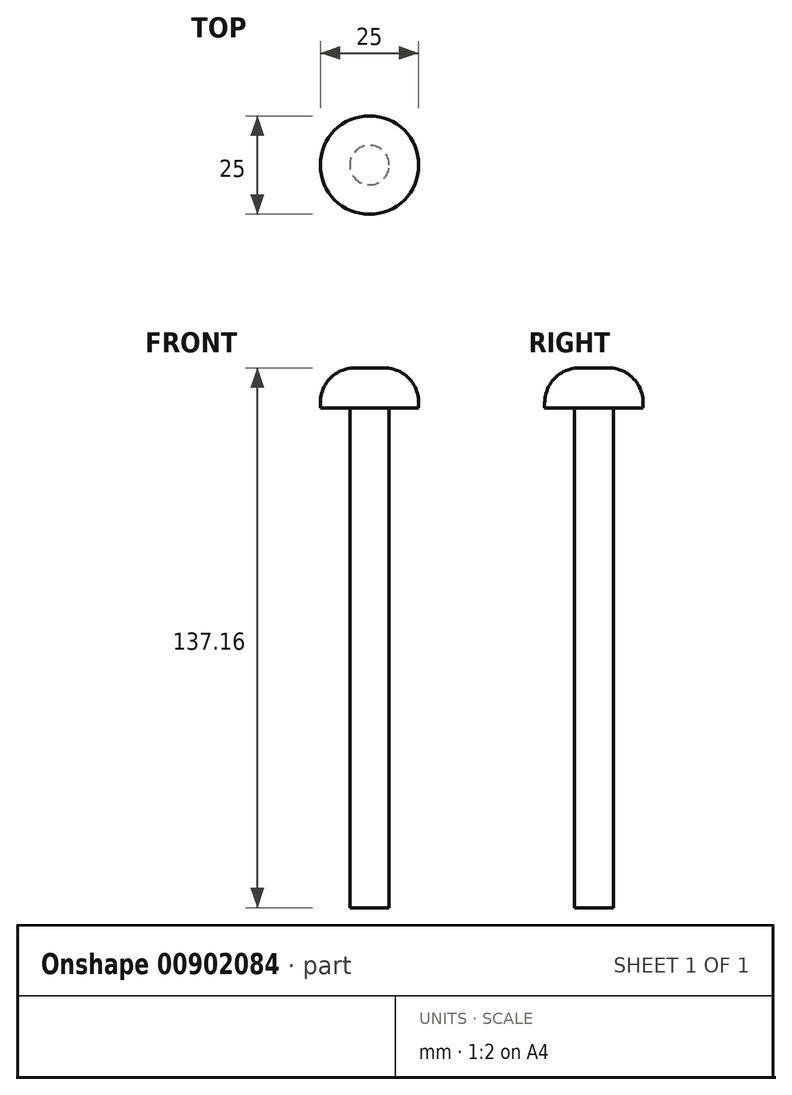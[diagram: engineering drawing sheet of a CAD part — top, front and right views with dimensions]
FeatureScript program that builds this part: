
annotation { "Feature Type Name" : "Feature", "Feature Type Description" : "" }
export const myFeature = defineFeature(function(context is Context, id is Id, definition is map)
    precondition{}
    {
        {
            var Q0;
            Q0=qCreatedBy(makeId("Top.planeOp"),FACE);
            var sketch = newSketch(context, id + "F0", { "sketchPlane" : qUnion([Q0])});
            skCircle(sketch, "E0", {"center": v(0, 0) * mm, "radius": 5 * mm});
            skSolve(sketch);
        }
        {
            var Q0;
            Q0=qSketchRegion(id+"F0",true);
            extrude(context, id + "F1", {"entities" : qUnion([Q0]), "depth" : 127 * mm, "offsetDistance" : 25.4 * mm});
        }
        {
            var Q0;
            Q0=makeQuery(id+"F1.opExtrude","CAP_FACE",FACE,{"disambiguationData":[OSD([sQuery(id+"F0.wireOp",EDGE,"E0")])],"isStart":false});
            var sketch = newSketch(context, id + "F2", { "sketchPlane" : qUnion([Q0])});
            skCircle(sketch, "E1", {"center": v(0, 0) * mm, "radius": 12.5 * mm});
            skSolve(sketch);
        }
        {
            var Q0;
            Q0=makeQuery(id+"F2.imprint","IMPRINT",FACE,{"disambiguationData":[TD([[makeQuery(id+"F2.imprint","IMPRINT",EDGE,{"derivedFrom":sQuery(id+"F2.wireOp",EDGE,"E1")}),1.0]])]});
            var Q1;
            Q1=makeQuery(id+"F2.imprint","IMPRINT",FACE,{"disambiguationData":[TD([[makeQuery(id+"F2.imprint","IMPRINT",EDGE,{"derivedFrom":makeQuery(id+"F1.opExtrude","CAP_EDGE",EDGE,{"disambiguationData":[OSD([sQuery(id+"F0.wireOp",EDGE,"E0")])],"isStart":false})}),1.0]])]});
            extrude(context, id + "F3", {"entities" : qUnion([Q0, Q1]), "operationType" : NewBodyOperationType.ADD, "depth" : 10.16 * mm, "offsetDistance" : 25.4 * mm});
        }
        {
            var Q0;
            Q0=makeQuery(id+"F3.opExtrude","CAP_EDGE",EDGE,{"disambiguationData":[OSD([sQuery(id+"F2.wireOp",EDGE,"E1")])],"isStart":false});
            fillet(context, id + "F4", {"entities" : qUnion([Q0]), "radius" : 8.9 * mm, "tangentPropagation" : true, "allowEdgeOverflow" : false});
        }
    });
